# Revit family: PTT 615,618,915,918
name_source: partatom
category: Windows
revit_build: Autodesk Revit LT 2016 (Build: 20150220_1215(x64)
units: mm (PartAtom-declared; Revit-internal decimal feet)

## family parameters
Always vertical = Yes
Cut with Voids When Loaded = No
Host = Wall
OmniClass Number = 23.30.20.00
OmniClass Title = Windows
Room Calculation Point = No
Shared = No

## types (4) — shared parameters
Aluminium anodized = Aluminium
Bottom guide = 33 mm
Default Sill Height = 914 mm
Description = Anodized Aluminium
Glazing = Glass
Height = 1510 mm  [stored 4.95407 ft]
Manufacturer = Robmeg
Plaster = 5 mm  [stored 0.0164042 ft]
Rough Height = 1219 mm
Side hung = Yes
Top hung = No
URL = http://www.robmeg.co.za
Wall Closure = By host

## per-type parameters (varying)
| type | Bottom Mullion height | Bottom glass thickness | Model | Top mulliion height | Width |
| PTT type- 915 | 300 mm | 4 mm  [stored 0.0131234 ft] | PTT 915 | 600 mm | 910 mm  [stored 2.98556 ft] |
| PTT Type- 918 | 500 mm  [stored 1.64042 ft] | 6 mm  [stored 0.019685 ft] | PTT 918 | 500 mm  [stored 1.64042 ft] | 910 mm  [stored 2.98556 ft] |
| PTT Type- 615 | 300 mm | 4 mm  [stored 0.0131234 ft] | PTT 615 | 600 mm | 610 mm  [stored 2.00131 ft] |
| PTT Type- 618 | 500 mm  [stored 1.64042 ft] | 6 mm  [stored 0.019685 ft] | PTT 618 | 500 mm  [stored 1.64042 ft] | 610 mm  [stored 2.00131 ft] |

note: [stored X ft] marks values corroborated as IEEE doubles in the binary element streams (Revit-internal decimal feet)

## geometry (parser evidence)
native form markers: Sweep x3
no freeform markers — native parametric forms only
